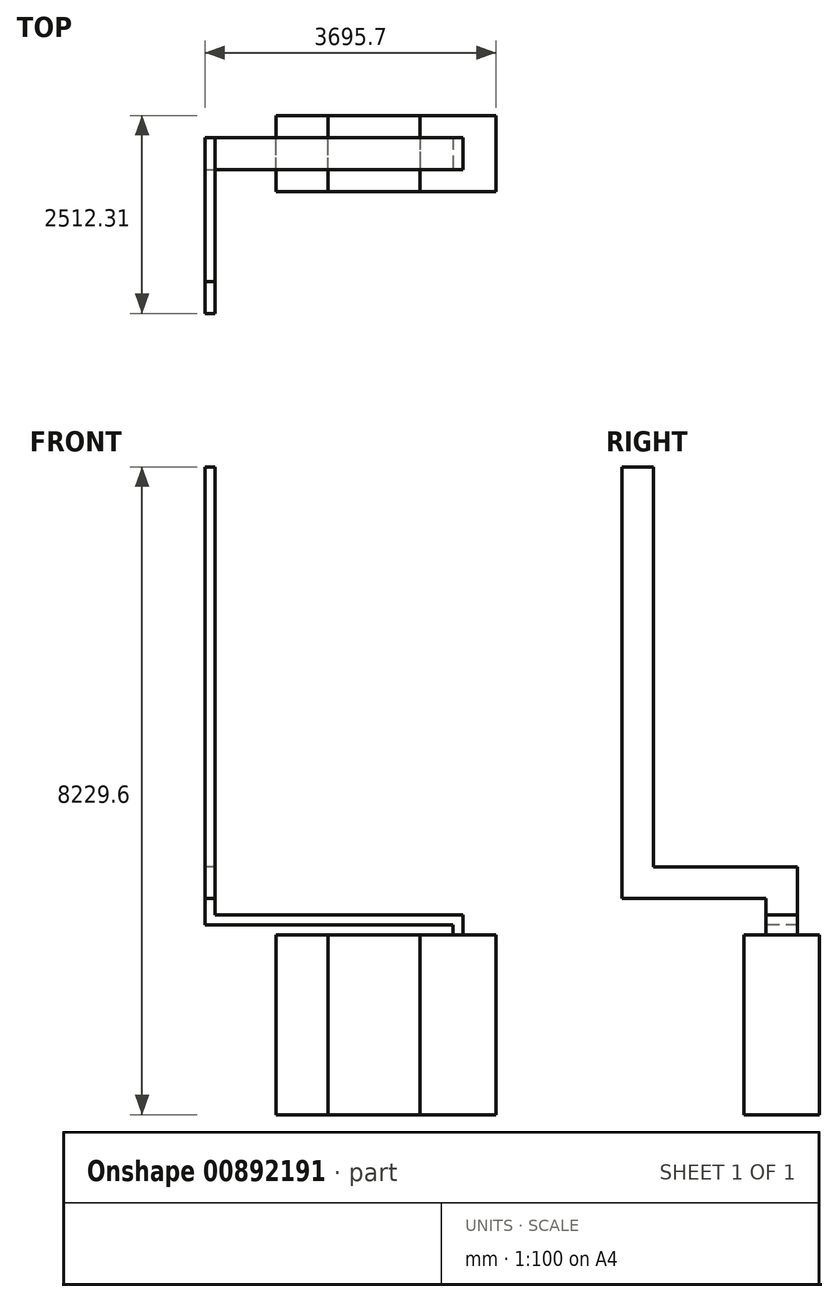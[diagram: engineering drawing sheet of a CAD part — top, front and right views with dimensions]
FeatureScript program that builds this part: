
annotation { "Feature Type Name" : "Feature", "Feature Type Description" : "" }
export const myFeature = defineFeature(function(context is Context, id is Id, definition is map)
    precondition{}
    {
        {
            var Q0;
            Q0=qCreatedBy(makeId("Top.planeOp"),FACE);
            var sketch = newSketch(context, id + "F0", { "sketchPlane" : qUnion([Q0])});
            skLineSegment(sketch, "E0.bottom", {"start": v(0, 0) * mm, "end": v(660.4, 0) * mm});
            skLineSegment(sketch, "E0.top", {"start": v(0, 965.2) * mm, "end": v(660.4, 965.2) * mm});
            skLineSegment(sketch, "E0.left", {"start": v(0, 0) * mm, "end": v(0, 965.2) * mm});
            skLineSegment(sketch, "E0.right", {"start": v(660.4, 0) * mm, "end": v(660.4, 965.2) * mm});
            skLineSegment(sketch, "E1.bottom", {"start": v(660.4, 965.2) * mm, "end": v(1828.8, 965.2) * mm});
            skLineSegment(sketch, "E1.top", {"start": v(660.4, 0) * mm, "end": v(1828.8, 0) * mm});
            skLineSegment(sketch, "E1.left", {"start": v(660.4, 965.2) * mm, "end": v(660.4, 0) * mm});
            skLineSegment(sketch, "E1.right", {"start": v(1828.8, 965.2) * mm, "end": v(1828.8, 0) * mm});
            skLineSegment(sketch, "E2.bottom", {"start": v(1828.8, 965.2) * mm, "end": v(2794, 965.2) * mm});
            skLineSegment(sketch, "E2.top", {"start": v(1828.8, 0) * mm, "end": v(2794, 0) * mm});
            skLineSegment(sketch, "E2.right", {"start": v(2794, 965.2) * mm, "end": v(2794, 0) * mm});
            skSolve(sketch);
        }
        {
            var Q0;
            Q0=makeQuery(id+"F0.imprint","IMPRINT",FACE,{"disambiguationData":[TD([[makeQuery(id+"F0.imprint","IMPRINT",EDGE,{"derivedFrom":sQuery(id+"F0.wireOp",EDGE,"E0.bottom")}),1.0]])]});
            extrude(context, id + "F1", {"entities" : qUnion([Q0]), "depth" : 2286 * mm, "offsetDistance" : 25.4 * mm});
        }
        {
            var Q0;
            Q0=makeQuery(id+"F0.imprint","IMPRINT",FACE,{"disambiguationData":[TD([[makeQuery(id+"F0.imprint","IMPRINT",EDGE,{"derivedFrom":sQuery(id+"F0.wireOp",EDGE,"E0.right")}),-1.0]])]});
            extrude(context, id + "F2", {"entities" : qUnion([Q0]), "depth" : 2286 * mm, "offsetDistance" : 25.4 * mm});
        }
        {
            var Q0;
            Q0=makeQuery(id+"F0.imprint","IMPRINT",FACE,{"disambiguationData":[TD([[makeQuery(id+"F0.imprint","IMPRINT",EDGE,{"derivedFrom":sQuery(id+"F0.wireOp",EDGE,"E1.right")}),1.0]])]});
            extrude(context, id + "F3", {"entities" : qUnion([Q0]), "depth" : 2286 * mm, "offsetDistance" : 25.4 * mm});
        }
        {
            var Q0;
            Q0=makeQuery(id+"F3.opExtrude","CAP_FACE",FACE,{"disambiguationData":[OSD([sQuery(id+"F0.wireOp",EDGE,"E1.right"),sQuery(id+"F0.wireOp",EDGE,"E2.bottom"),sQuery(id+"F0.wireOp",EDGE,"E2.top"),sQuery(id+"F0.wireOp",EDGE,"E2.right")])],"isStart":false});
            var sketch = newSketch(context, id + "F4", { "sketchPlane" : qUnion([Q0])});
            skLineSegment(sketch, "E3.bottom", {"start": v(2374.9, 281.69) * mm, "end": v(2247.9, 281.69) * mm});
            skLineSegment(sketch, "E3.top", {"start": v(2374.9, 683.51) * mm, "end": v(2247.9, 683.51) * mm});
            skLineSegment(sketch, "E3.left", {"start": v(2374.9, 281.69) * mm, "end": v(2374.9, 683.51) * mm});
            skLineSegment(sketch, "E3.right", {"start": v(2247.9, 281.69) * mm, "end": v(2247.9, 683.51) * mm});
            skPoint(sketch, "E3.middle", {"position": v(2311.4, 482.6) * mm});
            skPoint(sketch, "E3.middle.positionSnap0", {"position": v(1828.8, 482.6) * mm});
            skPoint(sketch, "E3.middle.positionSnap1", {"position": v(2311.4, 965.2) * mm});
            skPoint(sketch, "E3.centerSnap0", {"position": v(1828.8, 482.6) * mm});
            skPoint(sketch, "E3.centerSnap1", {"position": v(2311.4, 965.2) * mm});
            skSolve(sketch);
        }
        {
            var Q0;
            Q0 = qSketchRegion(id + "F4", true);
            extrude(context, id + "F5", {"entities" : qUnion([Q0]), "depth" : 254 * mm, "offsetDistance" : 25.4 * mm});
        }
        {
            var Q0;
            Q0=makeQuery(id+"F5.opExtrude","SWEPT_FACE",FACE,{"disambiguationData":[OSD([sQuery(id+"F4.wireOp",EDGE,"E3.right")])]});
            var sketch = newSketch(context, id + "F6", { "sketchPlane" : qUnion([Q0])});
            skLineSegment(sketch, "E4.bottom", {"start": v(-683.51, 2540) * mm, "end": v(-281.69, 2540) * mm});
            skLineSegment(sketch, "E4.top", {"start": v(-683.51, 2413) * mm, "end": v(-281.69, 2413) * mm});
            skLineSegment(sketch, "E4.left", {"start": v(-683.51, 2540) * mm, "end": v(-683.51, 2413) * mm});
            skLineSegment(sketch, "E4.right", {"start": v(-281.69, 2540) * mm, "end": v(-281.69, 2413) * mm});
            skSolve(sketch);
        }
        {
            var Q0;
            Q0 = qSketchRegion(id + "F6", true);
            extrude(context, id + "F7", {"entities" : qUnion([Q0]), "operationType" : NewBodyOperationType.ADD, "depth" : 3149.6 * mm, "offsetDistance" : 25.4 * mm});
        }
        {
            var Q0;
            Q0=makeQuery(id+"F7.boolean.opBoolean","MERGE",FACE,{"derivedFrom":[makeQuery(id+"F5.opExtrude","CAP_FACE",FACE,{"disambiguationData":[OSD([sQuery(id+"F4.wireOp",EDGE,"E3.bottom"),sQuery(id+"F4.wireOp",EDGE,"E3.top"),sQuery(id+"F4.wireOp",EDGE,"E3.left"),sQuery(id+"F4.wireOp",EDGE,"E3.right")])],"isStart":false}),makeQuery(id+"F7.opExtrude","SWEPT_FACE",FACE,{"disambiguationData":[OSD([sQuery(id+"F6.wireOp",EDGE,"E4.bottom")])]})]});
            var sketch = newSketch(context, id + "F8", { "sketchPlane" : qUnion([Q0])});
            skLineSegment(sketch, "E5.bottom", {"start": v(-901.7, 683.51) * mm, "end": v(-774.7, 683.51) * mm});
            skLineSegment(sketch, "E5.top", {"start": v(-901.7, 281.69) * mm, "end": v(-774.7, 281.69) * mm});
            skLineSegment(sketch, "E5.left", {"start": v(-901.7, 683.51) * mm, "end": v(-901.7, 281.69) * mm});
            skLineSegment(sketch, "E5.right", {"start": v(-774.7, 683.51) * mm, "end": v(-774.7, 281.69) * mm});
            skSolve(sketch);
        }
        {
            var Q0;
            Q0 = qSketchRegion(id + "F8", true);
            extrude(context, id + "F9", {"entities" : qUnion([Q0]), "operationType" : NewBodyOperationType.ADD, "depth" : 609.6 * mm, "offsetDistance" : 25.4 * mm});
        }
        {
            var Q0;
            Q0=makeQuery(id+"F9.boolean.opBoolean","MERGE",FACE,{"derivedFrom":[makeQuery(id+"F7.boolean.opBoolean","MERGE",FACE,{"derivedFrom":[makeQuery(id+"F5.opExtrude","SWEPT_FACE",FACE,{"disambiguationData":[OSD([sQuery(id+"F4.wireOp",EDGE,"E3.bottom")])]}),makeQuery(id+"F7.opExtrude","SWEPT_FACE",FACE,{"disambiguationData":[OSD([sQuery(id+"F6.wireOp",EDGE,"E4.right")])]})]}),makeQuery(id+"F9.opExtrude","SWEPT_FACE",FACE,{"disambiguationData":[OSD([sQuery(id+"F8.wireOp",EDGE,"E5.top")])]})]});
            var sketch = newSketch(context, id + "F10", { "sketchPlane" : qUnion([Q0])});
            skLineSegment(sketch, "E6.bottom", {"start": v(-901.7, 3149.6) * mm, "end": v(-774.7, 3149.6) * mm});
            skLineSegment(sketch, "E6.top", {"start": v(-901.7, 2747.77) * mm, "end": v(-774.7, 2747.77) * mm});
            skLineSegment(sketch, "E6.left", {"start": v(-901.7, 3149.6) * mm, "end": v(-901.7, 2747.77) * mm});
            skLineSegment(sketch, "E6.right", {"start": v(-774.7, 3149.6) * mm, "end": v(-774.7, 2747.77) * mm});
            skSolve(sketch);
        }
        {
            var Q0;
            Q0 = qSketchRegion(id + "F10", true);
            extrude(context, id + "F11", {"entities" : qUnion([Q0]), "operationType" : NewBodyOperationType.ADD, "depth" : 1828.8 * mm, "offsetDistance" : 25.4 * mm});
        }
        {
            var Q0;
            Q0=makeQuery(id+"F11.boolean.opBoolean","MERGE",FACE,{"derivedFrom":[makeQuery(id+"F9.opExtrude","CAP_FACE",FACE,{"disambiguationData":[OSD([sQuery(id+"F8.wireOp",EDGE,"E5.bottom"),sQuery(id+"F8.wireOp",EDGE,"E5.top"),sQuery(id+"F8.wireOp",EDGE,"E5.left"),sQuery(id+"F8.wireOp",EDGE,"E5.right")])],"isStart":false}),makeQuery(id+"F11.opExtrude","SWEPT_FACE",FACE,{"disambiguationData":[OSD([sQuery(id+"F10.wireOp",EDGE,"E6.bottom")])]})]});
            var sketch = newSketch(context, id + "F12", { "sketchPlane" : qUnion([Q0])});
            skLineSegment(sketch, "E7.bottom", {"start": v(-774.7, -1547.11) * mm, "end": v(-901.7, -1547.11) * mm});
            skLineSegment(sketch, "E7.top", {"start": v(-774.7, -1145.29) * mm, "end": v(-901.7, -1145.29) * mm});
            skLineSegment(sketch, "E7.left", {"start": v(-774.7, -1547.11) * mm, "end": v(-774.7, -1145.29) * mm});
            skLineSegment(sketch, "E7.right", {"start": v(-901.7, -1547.11) * mm, "end": v(-901.7, -1145.29) * mm});
            skSolve(sketch);
        }
        {
            var Q0;
            Q0=makeQuery(id+"F12.imprint","IMPRINT",FACE,{"disambiguationData":[TD([[makeQuery(id+"F12.imprint","IMPRINT",EDGE,{"derivedFrom":sQuery(id+"F12.wireOp",EDGE,"E7.bottom")}),-1.0]])]});
            extrude(context, id + "F13", {"entities" : qUnion([Q0]), "operationType" : NewBodyOperationType.ADD, "depth" : 5080 * mm, "offsetDistance" : 25.4 * mm});
        }
    });
